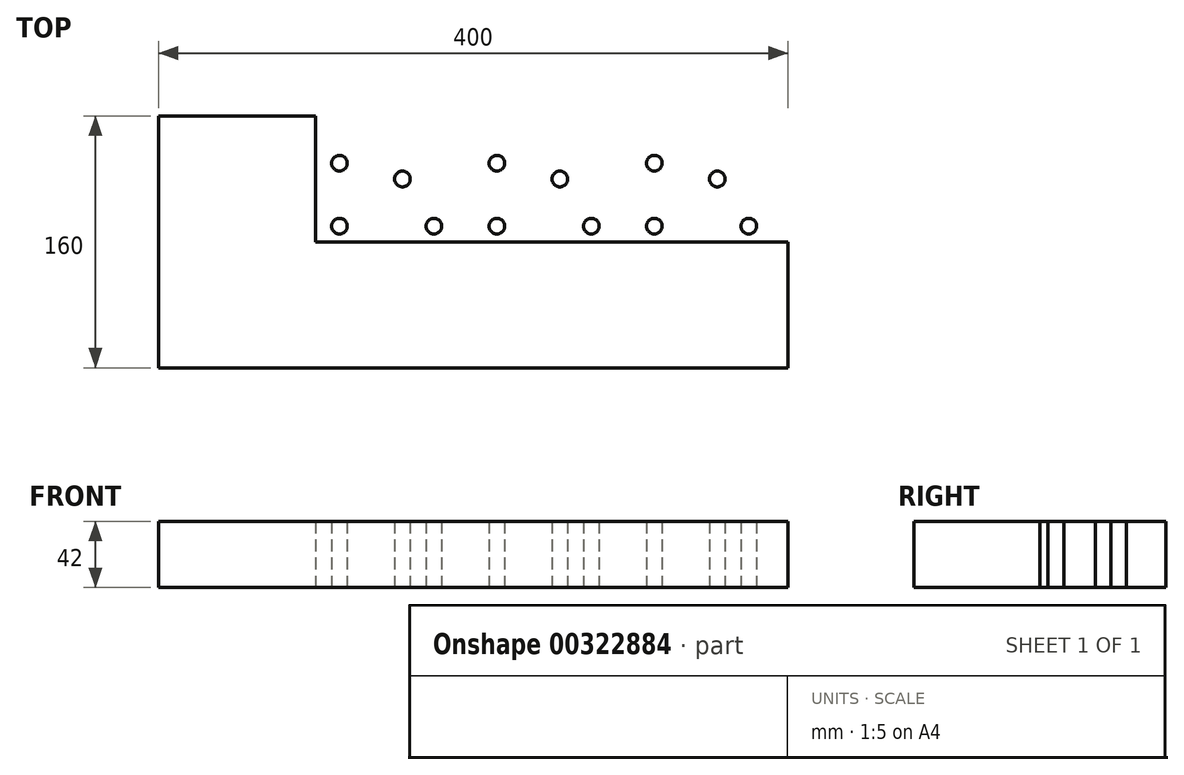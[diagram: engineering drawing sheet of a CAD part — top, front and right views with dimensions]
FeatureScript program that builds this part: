
annotation { "Feature Type Name" : "Feature", "Feature Type Description" : "" }
export const myFeature = defineFeature(function(context is Context, id is Id, definition is map)
    precondition{}
    {
        {
            var Q0;
            Q0=qCreatedBy(makeId("Top.planeOp"),FACE);
            var sketch = newSketch(context, id + "F0", { "sketchPlane" : qUnion([Q0])});
            skLineSegment(sketch, "E0.bottom", {"start": v(0, 80) * mm, "end": v(100, 80) * mm});
            skLineSegment(sketch, "E0.top", {"start": v(0, 0) * mm, "end": v(100, 0) * mm});
            skLineSegment(sketch, "E0.left", {"start": v(0, 80) * mm, "end": v(0, 0) * mm});
            skLineSegment(sketch, "E0.right", {"start": v(100, 80) * mm, "end": v(100, 0) * mm});
            skCircle(sketch, "E1", {"center": v(15, 50) * mm, "radius": 5 * mm});
            skCircle(sketch, "E2", {"center": v(15, 10) * mm, "radius": 5 * mm});
            skCircle(sketch, "E3", {"center": v(75, 10) * mm, "radius": 5 * mm});
            skCircle(sketch, "E4", {"center": v(55, 40) * mm, "radius": 5 * mm});
            skLineSegment(sketch, "E5.0.1.1", {"start": v(0, 160) * mm, "end": v(100, 160) * mm});
            skLineSegment(sketch, "E5.0.1.2", {"start": v(100, 160) * mm, "end": v(100, 80) * mm});
            skLineSegment(sketch, "E5.0.1.3", {"start": v(0, 160) * mm, "end": v(0, 80) * mm});
            skCircle(sketch, "E5.0.1.4", {"center": v(15, 90) * mm, "radius": 5 * mm});
            skCircle(sketch, "E5.0.1.5", {"center": v(15, 130) * mm, "radius": 5 * mm});
            skCircle(sketch, "E5.0.1.6", {"center": v(75, 90) * mm, "radius": 5 * mm});
            skCircle(sketch, "E5.0.1.7", {"center": v(55, 120) * mm, "radius": 5 * mm});
            skLineSegment(sketch, "E5.1.0.0", {"start": v(100, 0) * mm, "end": v(200, 0) * mm});
            skLineSegment(sketch, "E5.1.0.1", {"start": v(100, 80) * mm, "end": v(200, 80) * mm});
            skLineSegment(sketch, "E5.1.0.2", {"start": v(200, 80) * mm, "end": v(200, 0) * mm});
            skCircle(sketch, "E5.1.0.4", {"center": v(115, 10) * mm, "radius": 5 * mm});
            skCircle(sketch, "E5.1.0.5", {"center": v(115, 50) * mm, "radius": 5 * mm});
            skCircle(sketch, "E5.1.0.6", {"center": v(175, 10) * mm, "radius": 5 * mm});
            skCircle(sketch, "E5.1.0.7", {"center": v(155, 40) * mm, "radius": 5 * mm});
            skLineSegment(sketch, "E5.1.1.0", {"start": v(100, 80) * mm, "end": v(200, 80) * mm});
            skLineSegment(sketch, "E5.1.1.1", {"start": v(100, 160) * mm, "end": v(200, 160) * mm});
            skLineSegment(sketch, "E5.1.1.2", {"start": v(200, 160) * mm, "end": v(200, 80) * mm});
            skLineSegment(sketch, "E5.1.1.3", {"start": v(100, 160) * mm, "end": v(100, 80) * mm});
            skCircle(sketch, "E5.1.1.4", {"center": v(115, 90) * mm, "radius": 5 * mm});
            skCircle(sketch, "E5.1.1.5", {"center": v(115, 130) * mm, "radius": 5 * mm});
            skCircle(sketch, "E5.1.1.6", {"center": v(175, 90) * mm, "radius": 5 * mm});
            skCircle(sketch, "E5.1.1.7", {"center": v(155, 120) * mm, "radius": 5 * mm});
            skLineSegment(sketch, "E5.2.0.0", {"start": v(200, 0) * mm, "end": v(300, 0) * mm});
            skLineSegment(sketch, "E5.2.0.1", {"start": v(200, 80) * mm, "end": v(300, 80) * mm});
            skLineSegment(sketch, "E5.2.0.2", {"start": v(300, 80) * mm, "end": v(300, 0) * mm});
            skLineSegment(sketch, "E5.2.0.3", {"start": v(200, 80) * mm, "end": v(200, 0) * mm});
            skCircle(sketch, "E5.2.0.4", {"center": v(215, 10) * mm, "radius": 5 * mm});
            skCircle(sketch, "E5.2.0.5", {"center": v(215, 50) * mm, "radius": 5 * mm});
            skCircle(sketch, "E5.2.0.6", {"center": v(275, 10) * mm, "radius": 5 * mm});
            skCircle(sketch, "E5.2.0.7", {"center": v(255, 40) * mm, "radius": 5 * mm});
            skLineSegment(sketch, "E5.2.1.0", {"start": v(200, 80) * mm, "end": v(300, 80) * mm});
            skLineSegment(sketch, "E5.2.1.1", {"start": v(200, 160) * mm, "end": v(300, 160) * mm});
            skLineSegment(sketch, "E5.2.1.2", {"start": v(300, 160) * mm, "end": v(300, 80) * mm});
            skLineSegment(sketch, "E5.2.1.3", {"start": v(200, 160) * mm, "end": v(200, 80) * mm});
            skCircle(sketch, "E5.2.1.4", {"center": v(215, 90) * mm, "radius": 5 * mm});
            skCircle(sketch, "E5.2.1.5", {"center": v(215, 130) * mm, "radius": 5 * mm});
            skCircle(sketch, "E5.2.1.6", {"center": v(275, 90) * mm, "radius": 5 * mm});
            skCircle(sketch, "E5.2.1.7", {"center": v(255, 120) * mm, "radius": 5 * mm});
            skLineSegment(sketch, "E5.3.0.0", {"start": v(300, 0) * mm, "end": v(400, 0) * mm});
            skLineSegment(sketch, "E5.3.0.1", {"start": v(300, 80) * mm, "end": v(400, 80) * mm});
            skLineSegment(sketch, "E5.3.0.2", {"start": v(400, 80) * mm, "end": v(400, 0) * mm});
            skLineSegment(sketch, "E5.3.0.3", {"start": v(300, 80) * mm, "end": v(300, 0) * mm});
            skCircle(sketch, "E5.3.0.4", {"center": v(315, 10) * mm, "radius": 5 * mm});
            skCircle(sketch, "E5.3.0.5", {"center": v(315, 50) * mm, "radius": 5 * mm});
            skCircle(sketch, "E5.3.0.6", {"center": v(375, 10) * mm, "radius": 5 * mm});
            skCircle(sketch, "E5.3.0.7", {"center": v(355, 40) * mm, "radius": 5 * mm});
            skLineSegment(sketch, "E5.3.1.0", {"start": v(300, 80) * mm, "end": v(400, 80) * mm});
            skLineSegment(sketch, "E5.3.1.1", {"start": v(300, 160) * mm, "end": v(400, 160) * mm});
            skLineSegment(sketch, "E5.3.1.2", {"start": v(400, 160) * mm, "end": v(400, 80) * mm});
            skLineSegment(sketch, "E5.3.1.3", {"start": v(300, 160) * mm, "end": v(300, 80) * mm});
            skCircle(sketch, "E5.3.1.4", {"center": v(315, 90) * mm, "radius": 5 * mm});
            skCircle(sketch, "E5.3.1.5", {"center": v(315, 130) * mm, "radius": 5 * mm});
            skCircle(sketch, "E5.3.1.6", {"center": v(375, 90) * mm, "radius": 5 * mm});
            skCircle(sketch, "E5.3.1.7", {"center": v(355, 120) * mm, "radius": 5 * mm});
            skLineSegment(sketch, "E5.direction1", {"start": v(0, 0) * mm, "end": v(100, 0) * mm, "construction": true});
            skLineSegment(sketch, "E5.direction2", {"start": v(0, 0) * mm, "end": v(0, 80) * mm, "construction": true});
            skSolve(sketch);
        }
        {
            var Q0;
            Q0=makeQuery(id+"F0.imprint","IMPRINT",FACE,{"disambiguationData":[TD([[makeQuery(id+"F0.imprint","IMPRINT",EDGE,{"derivedFrom":sQuery(id+"F0.wireOp",EDGE,"E5.1.1.7")}),1.0]])]});
            var Q1;
            Q1=makeQuery(id+"F0.imprint","IMPRINT",FACE,{"disambiguationData":[TD([[makeQuery(id+"F0.imprint","IMPRINT",EDGE,{"derivedFrom":sQuery(id+"F0.wireOp",EDGE,"E5.3.1.5")}),1.0]])]});
            var Q2;
            Q2=makeQuery(id+"F0.imprint","IMPRINT",FACE,{"disambiguationData":[TD([[makeQuery(id+"F0.imprint","IMPRINT",EDGE,{"derivedFrom":sQuery(id+"F0.wireOp",EDGE,"E1")}),1.0]])]});
            var Q3;
            Q3=makeQuery(id+"F0.imprint","IMPRINT",FACE,{"disambiguationData":[TD([[makeQuery(id+"F0.imprint","IMPRINT",EDGE,{"derivedFrom":sQuery(id+"F0.wireOp",EDGE,"E5.1.0.0")}),1.0]])]});
            var Q4;
            Q4=makeQuery(id+"F0.imprint","IMPRINT",FACE,{"disambiguationData":[TD([[makeQuery(id+"F0.imprint","IMPRINT",EDGE,{"derivedFrom":sQuery(id+"F0.wireOp",EDGE,"E0.top")}),1.0]])]});
            var Q5;
            Q5=makeQuery(id+"F0.imprint","IMPRINT",FACE,{"disambiguationData":[TD([[makeQuery(id+"F0.imprint","IMPRINT",EDGE,{"derivedFrom":sQuery(id+"F0.wireOp",EDGE,"E5.2.0.0")}),1.0]])]});
            var Q6;
            Q6=makeQuery(id+"F0.imprint","IMPRINT",FACE,{"disambiguationData":[TD([[makeQuery(id+"F0.imprint","IMPRINT",EDGE,{"derivedFrom":sQuery(id+"F0.wireOp",EDGE,"E5.0.1.5")}),1.0]])]});
            var Q7;
            Q7=makeQuery(id+"F0.imprint","IMPRINT",FACE,{"disambiguationData":[TD([[makeQuery(id+"F0.imprint","IMPRINT",EDGE,{"derivedFrom":sQuery(id+"F0.wireOp",EDGE,"E5.1.1.5")}),1.0]])]});
            var Q8;
            Q8=makeQuery(id+"F0.imprint","IMPRINT",FACE,{"disambiguationData":[TD([[makeQuery(id+"F0.imprint","IMPRINT",EDGE,{"derivedFrom":sQuery(id+"F0.wireOp",EDGE,"E5.3.1.0")}),1.0]])]});
            var Q9;
            Q9=makeQuery(id+"F0.imprint","IMPRINT",FACE,{"disambiguationData":[TD([[makeQuery(id+"F0.imprint","IMPRINT",EDGE,{"derivedFrom":sQuery(id+"F0.wireOp",EDGE,"E5.1.0.7")}),1.0]])]});
            var Q10;
            Q10=makeQuery(id+"F0.imprint","IMPRINT",FACE,{"disambiguationData":[TD([[makeQuery(id+"F0.imprint","IMPRINT",EDGE,{"derivedFrom":sQuery(id+"F0.wireOp",EDGE,"E5.2.1.0")}),1.0]])]});
            var Q11;
            Q11=makeQuery(id+"F0.imprint","IMPRINT",FACE,{"disambiguationData":[TD([[makeQuery(id+"F0.imprint","IMPRINT",EDGE,{"derivedFrom":sQuery(id+"F0.wireOp",EDGE,"E5.2.1.5")}),1.0]])]});
            var Q12;
            Q12=makeQuery(id+"F0.imprint","IMPRINT",FACE,{"disambiguationData":[TD([[makeQuery(id+"F0.imprint","IMPRINT",EDGE,{"derivedFrom":sQuery(id+"F0.wireOp",EDGE,"E5.1.1.0")}),1.0]])]});
            var Q13;
            Q13=makeQuery(id+"F0.imprint","IMPRINT",FACE,{"disambiguationData":[TD([[makeQuery(id+"F0.imprint","IMPRINT",EDGE,{"derivedFrom":sQuery(id+"F0.wireOp",EDGE,"E0.bottom")}),1.0]])]});
            var Q14;
            Q14=makeQuery(id+"F0.imprint","IMPRINT",FACE,{"disambiguationData":[TD([[makeQuery(id+"F0.imprint","IMPRINT",EDGE,{"derivedFrom":sQuery(id+"F0.wireOp",EDGE,"E5.3.1.4")}),1.0]])]});
            var Q15;
            Q15=makeQuery(id+"F0.imprint","IMPRINT",FACE,{"disambiguationData":[TD([[makeQuery(id+"F0.imprint","IMPRINT",EDGE,{"derivedFrom":sQuery(id+"F0.wireOp",EDGE,"E5.3.0.4")}),1.0]])]});
            var Q16;
            Q16=makeQuery(id+"F0.imprint","IMPRINT",FACE,{"disambiguationData":[TD([[makeQuery(id+"F0.imprint","IMPRINT",EDGE,{"derivedFrom":sQuery(id+"F0.wireOp",EDGE,"E5.3.0.0")}),1.0]])]});
            var Q17;
            Q17=makeQuery(id+"F0.imprint","IMPRINT",FACE,{"disambiguationData":[TD([[makeQuery(id+"F0.imprint","IMPRINT",EDGE,{"derivedFrom":sQuery(id+"F0.wireOp",EDGE,"E5.3.0.5")}),1.0]])]});
            var Q18;
            Q18=makeQuery(id+"F0.imprint","IMPRINT",FACE,{"disambiguationData":[TD([[makeQuery(id+"F0.imprint","IMPRINT",EDGE,{"derivedFrom":sQuery(id+"F0.wireOp",EDGE,"E5.2.0.7")}),1.0]])]});
            var Q19;
            Q19=makeQuery(id+"F0.imprint","IMPRINT",FACE,{"disambiguationData":[TD([[makeQuery(id+"F0.imprint","IMPRINT",EDGE,{"derivedFrom":sQuery(id+"F0.wireOp",EDGE,"E2")}),1.0]])]});
            var Q20;
            Q20=makeQuery(id+"F0.imprint","IMPRINT",FACE,{"disambiguationData":[TD([[makeQuery(id+"F0.imprint","IMPRINT",EDGE,{"derivedFrom":sQuery(id+"F0.wireOp",EDGE,"E3")}),1.0]])]});
            var Q21;
            Q21=makeQuery(id+"F0.imprint","IMPRINT",FACE,{"disambiguationData":[TD([[makeQuery(id+"F0.imprint","IMPRINT",EDGE,{"derivedFrom":sQuery(id+"F0.wireOp",EDGE,"E4")}),1.0]])]});
            var Q22;
            Q22=makeQuery(id+"F0.imprint","IMPRINT",FACE,{"disambiguationData":[TD([[makeQuery(id+"F0.imprint","IMPRINT",EDGE,{"derivedFrom":sQuery(id+"F0.wireOp",EDGE,"E5.2.1.4")}),1.0]])]});
            var Q23;
            Q23=makeQuery(id+"F0.imprint","IMPRINT",FACE,{"disambiguationData":[TD([[makeQuery(id+"F0.imprint","IMPRINT",EDGE,{"derivedFrom":sQuery(id+"F0.wireOp",EDGE,"E5.2.1.6")}),1.0]])]});
            var Q24;
            Q24=makeQuery(id+"F0.imprint","IMPRINT",FACE,{"disambiguationData":[TD([[makeQuery(id+"F0.imprint","IMPRINT",EDGE,{"derivedFrom":sQuery(id+"F0.wireOp",EDGE,"E5.0.1.4")}),1.0]])]});
            var Q25;
            Q25=makeQuery(id+"F0.imprint","IMPRINT",FACE,{"disambiguationData":[TD([[makeQuery(id+"F0.imprint","IMPRINT",EDGE,{"derivedFrom":sQuery(id+"F0.wireOp",EDGE,"E5.0.1.6")}),1.0]])]});
            var Q26;
            Q26=makeQuery(id+"F0.imprint","IMPRINT",FACE,{"disambiguationData":[TD([[makeQuery(id+"F0.imprint","IMPRINT",EDGE,{"derivedFrom":sQuery(id+"F0.wireOp",EDGE,"E5.3.0.6")}),1.0]])]});
            var Q27;
            Q27=makeQuery(id+"F0.imprint","IMPRINT",FACE,{"disambiguationData":[TD([[makeQuery(id+"F0.imprint","IMPRINT",EDGE,{"derivedFrom":sQuery(id+"F0.wireOp",EDGE,"E5.2.0.4")}),1.0]])]});
            var Q28;
            Q28=makeQuery(id+"F0.imprint","IMPRINT",FACE,{"disambiguationData":[TD([[makeQuery(id+"F0.imprint","IMPRINT",EDGE,{"derivedFrom":sQuery(id+"F0.wireOp",EDGE,"E5.1.1.6")}),1.0]])]});
            var Q29;
            Q29=makeQuery(id+"F0.imprint","IMPRINT",FACE,{"disambiguationData":[TD([[makeQuery(id+"F0.imprint","IMPRINT",EDGE,{"derivedFrom":sQuery(id+"F0.wireOp",EDGE,"E5.0.1.7")}),1.0]])]});
            var Q30;
            Q30=makeQuery(id+"F0.imprint","IMPRINT",FACE,{"disambiguationData":[TD([[makeQuery(id+"F0.imprint","IMPRINT",EDGE,{"derivedFrom":sQuery(id+"F0.wireOp",EDGE,"E5.1.0.4")}),1.0]])]});
            var Q31;
            Q31=makeQuery(id+"F0.imprint","IMPRINT",FACE,{"disambiguationData":[TD([[makeQuery(id+"F0.imprint","IMPRINT",EDGE,{"derivedFrom":sQuery(id+"F0.wireOp",EDGE,"E5.1.0.5")}),1.0]])]});
            var Q32;
            Q32=makeQuery(id+"F0.imprint","IMPRINT",FACE,{"disambiguationData":[TD([[makeQuery(id+"F0.imprint","IMPRINT",EDGE,{"derivedFrom":sQuery(id+"F0.wireOp",EDGE,"E5.1.0.6")}),1.0]])]});
            var Q33;
            Q33=makeQuery(id+"F0.imprint","IMPRINT",FACE,{"disambiguationData":[TD([[makeQuery(id+"F0.imprint","IMPRINT",EDGE,{"derivedFrom":sQuery(id+"F0.wireOp",EDGE,"E5.1.1.4")}),1.0]])]});
            var Q34;
            Q34=makeQuery(id+"F0.imprint","IMPRINT",FACE,{"disambiguationData":[TD([[makeQuery(id+"F0.imprint","IMPRINT",EDGE,{"derivedFrom":sQuery(id+"F0.wireOp",EDGE,"E5.3.0.7")}),1.0]])]});
            var Q35;
            Q35=makeQuery(id+"F0.imprint","IMPRINT",FACE,{"disambiguationData":[TD([[makeQuery(id+"F0.imprint","IMPRINT",EDGE,{"derivedFrom":sQuery(id+"F0.wireOp",EDGE,"E5.2.1.7")}),1.0]])]});
            var Q36;
            Q36=makeQuery(id+"F0.imprint","IMPRINT",FACE,{"disambiguationData":[TD([[makeQuery(id+"F0.imprint","IMPRINT",EDGE,{"derivedFrom":sQuery(id+"F0.wireOp",EDGE,"E5.3.1.6")}),1.0]])]});
            var Q37;
            Q37=makeQuery(id+"F0.imprint","IMPRINT",FACE,{"disambiguationData":[TD([[makeQuery(id+"F0.imprint","IMPRINT",EDGE,{"derivedFrom":sQuery(id+"F0.wireOp",EDGE,"E5.2.0.5")}),1.0]])]});
            var Q38;
            Q38=makeQuery(id+"F0.imprint","IMPRINT",FACE,{"disambiguationData":[TD([[makeQuery(id+"F0.imprint","IMPRINT",EDGE,{"derivedFrom":sQuery(id+"F0.wireOp",EDGE,"E5.2.0.6")}),1.0]])]});
            var Q39;
            Q39=makeQuery(id+"F0.imprint","IMPRINT",FACE,{"disambiguationData":[TD([[makeQuery(id+"F0.imprint","IMPRINT",EDGE,{"derivedFrom":sQuery(id+"F0.wireOp",EDGE,"E5.3.1.7")}),1.0]])]});
            extrude(context, id + "F1", {"entities" : qUnion([Q0, Q1, Q2, Q3, Q4, Q5, Q6, Q7, Q8, Q9, Q10, Q11, Q12, Q13, Q14, Q15, Q16, Q17, Q18, Q19, Q20, Q21, Q22, Q23, Q24, Q25, Q26, Q27, Q28, Q29, Q30, Q31, Q32, Q33, Q34, Q35, Q36, Q37, Q38, Q39]), "depth" : 42 * mm});
        }
    });
